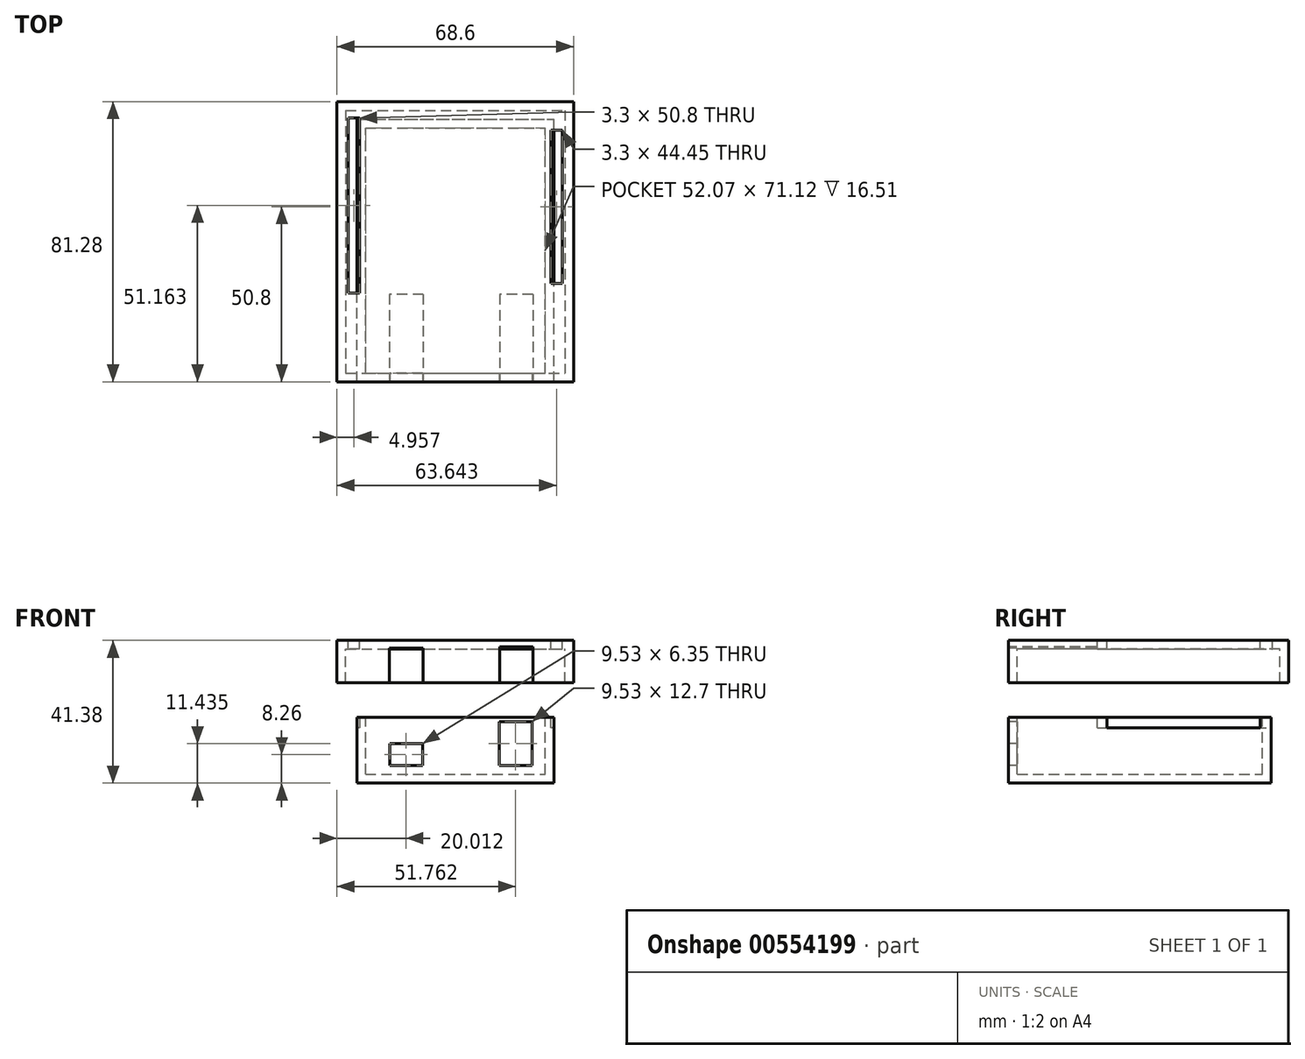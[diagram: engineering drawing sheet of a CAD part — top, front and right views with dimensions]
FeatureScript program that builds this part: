
annotation { "Feature Type Name" : "Feature", "Feature Type Description" : "" }
export const myFeature = defineFeature(function(context is Context, id is Id, definition is map)
    precondition{}
    {
        {
            var Q0;
            Q0=qCreatedBy(makeId("Front.planeOp"),FACE);
            var sketch = newSketch(context, id + "F0", { "sketchPlane" : qUnion([Q0])});
            skLineSegment(sketch, "E0.bottom", {"start": v(-28.58, -9.52) * mm, "end": v(28.58, -9.52) * mm});
            skLineSegment(sketch, "E0.top", {"start": v(-28.58, 9.52) * mm, "end": v(28.58, 9.52) * mm});
            skLineSegment(sketch, "E0.left", {"start": v(-28.58, -9.52) * mm, "end": v(-28.58, 9.52) * mm});
            skLineSegment(sketch, "E0.right", {"start": v(28.58, -9.52) * mm, "end": v(28.58, 9.52) * mm});
            skPoint(sketch, "E0.middle", {"position": v(0, 0) * mm});
            skSolve(sketch);
        }
        {
            var Q0;
            Q0 = qSketchRegion(id + "F0", true);
            extrude(context, id + "F1", {"entities" : qUnion([Q0]), "depth" : 76.2 * mm, "offsetDistance" : 25.4 * mm});
        }
        {
            var Q0;
            Q0=makeQuery(id+"F1.opExtrude","SWEPT_FACE",FACE,{"disambiguationData":[OSD([sQuery(id+"F0.wireOp",EDGE,"E0.top")])]});
            shell(context, id + "F2", {"entities" : qUnion([Q0]), "thickness" : 2.54 * mm});
        }
        {
            var Q0;
            Q0=makeQuery(id+"F1.opExtrude","CAP_FACE",FACE,{"disambiguationData":[OSD([sQuery(id+"F0.wireOp",EDGE,"E0.bottom"),sQuery(id+"F0.wireOp",EDGE,"E0.top"),sQuery(id+"F0.wireOp",EDGE,"E0.left"),sQuery(id+"F0.wireOp",EDGE,"E0.right")])],"isStart":false});
            var sketch = newSketch(context, id + "F3", { "sketchPlane" : qUnion([Q0])});
            skLineSegment(sketch, "E1.bottom", {"start": v(-9.53, -4.44) * mm, "end": v(-19.05, -4.44) * mm});
            skLineSegment(sketch, "E1.top", {"start": v(-9.53, 1.9) * mm, "end": v(-19.05, 1.9) * mm});
            skLineSegment(sketch, "E1.left", {"start": v(-9.53, -4.44) * mm, "end": v(-9.53, 1.9) * mm});
            skLineSegment(sketch, "E1.right", {"start": v(-19.05, -4.44) * mm, "end": v(-19.05, 1.9) * mm});
            skPoint(sketch, "E1.middle", {"position": v(-14.29, -1.27) * mm});
            skSolve(sketch);
        }
        {
            var Q0;
            Q0=makeQuery(id+"F3.imprint","IMPRINT",FACE,{"disambiguationData":[TD([[makeQuery(id+"F3.imprint","IMPRINT",EDGE,{"derivedFrom":sQuery(id+"F3.wireOp",EDGE,"E1.bottom")}),-1.0]])]});
            extrude(context, id + "F4", {"entities" : qUnion([Q0]), "operationType" : NewBodyOperationType.REMOVE, "oppositeDirection" : true, "depth" : 25.4 * mm, "offsetDistance" : 25.4 * mm});
        }
        {
            var Q0;
            Q0=makeQuery(id+"F1.opExtrude","CAP_FACE",FACE,{"disambiguationData":[OSD([sQuery(id+"F0.wireOp",EDGE,"E0.bottom"),sQuery(id+"F0.wireOp",EDGE,"E0.top"),sQuery(id+"F0.wireOp",EDGE,"E0.left"),sQuery(id+"F0.wireOp",EDGE,"E0.right")])],"isStart":false});
            var sketch = newSketch(context, id + "F5", { "sketchPlane" : qUnion([Q0])});
            skLineSegment(sketch, "E2.bottom", {"start": v(12.7, 8.26) * mm, "end": v(22.23, 8.26) * mm});
            skLineSegment(sketch, "E2.top", {"start": v(12.7, -4.44) * mm, "end": v(22.23, -4.44) * mm});
            skLineSegment(sketch, "E2.left", {"start": v(12.7, 8.26) * mm, "end": v(12.7, -4.44) * mm});
            skLineSegment(sketch, "E2.right", {"start": v(22.22, 8.26) * mm, "end": v(22.23, -4.44) * mm});
            skPoint(sketch, "E2.middle", {"position": v(17.46, 1.9) * mm});
            skSolve(sketch);
        }
        {
            var Q0;
            Q0=makeQuery(id+"F5.imprint","IMPRINT",FACE,{"disambiguationData":[TD([[makeQuery(id+"F5.imprint","IMPRINT",EDGE,{"derivedFrom":sQuery(id+"F5.wireOp",EDGE,"E2.bottom")}),-1.0]])]});
            extrude(context, id + "F6", {"entities" : qUnion([Q0]), "operationType" : NewBodyOperationType.REMOVE, "oppositeDirection" : true, "depth" : 25.4 * mm, "offsetDistance" : 25.4 * mm});
        }
        {
            var Q0;
            Q0=makeQuery(id+"F1.opExtrude","CAP_FACE",FACE,{"disambiguationData":[OSD([sQuery(id+"F0.wireOp",EDGE,"E0.bottom"),sQuery(id+"F0.wireOp",EDGE,"E0.top"),sQuery(id+"F0.wireOp",EDGE,"E0.left"),sQuery(id+"F0.wireOp",EDGE,"E0.right")])],"isStart":false});
            var sketch = newSketch(context, id + "F7", { "sketchPlane" : qUnion([Q0])});
            skLineSegment(sketch, "E3", {"start": v(0, 0) * mm, "end": v(0, 0) * mm});
            skSolve(sketch);
        }
        {
            var Q0;
            Q0=makeQuery(id+"F7.imprint","IMPRINT",FACE,{"disambiguationData":[TD([[makeQuery(id+"F7.imprint","IMPRINT",EDGE,{"derivedFrom":makeQuery(id+"F1.opExtrude","CAP_EDGE",EDGE,{"disambiguationData":[OSD([sQuery(id+"F0.wireOp",EDGE,"E0.bottom")])],"isStart":false})}),1.0]])]});
            var sketch = newSketch(context, id + "F8", { "sketchPlane" : qUnion([Q0])});
            skLineSegment(sketch, "E4.bottom", {"start": v(-34.3, 19.6) * mm, "end": v(34.3, 19.6) * mm});
            skLineSegment(sketch, "E4.top", {"start": v(-34.3, 31.85) * mm, "end": v(34.3, 31.85) * mm});
            skLineSegment(sketch, "E4.left", {"start": v(-34.3, 19.6) * mm, "end": v(-34.3, 31.85) * mm});
            skLineSegment(sketch, "E4.right", {"start": v(34.3, 19.6) * mm, "end": v(34.3, 31.85) * mm});
            skPoint(sketch, "E4.middle", {"position": v(0, 25.72) * mm});
            skSolve(sketch);
        }
        {
            var Q0;
            Q0 = qSketchRegion(id + "F8", true);
            extrude(context, id + "F9", {"entities" : qUnion([Q0]), "oppositeDirection" : true, "depth" : 81.28 * mm, "offsetDistance" : 25.4 * mm});
        }
        {
            var Q0;
            Q0=makeQuery(id+"F9.opExtrude","SWEPT_FACE",FACE,{"disambiguationData":[OSD([sQuery(id+"F8.wireOp",EDGE,"E4.bottom")])]});
            shell(context, id + "F10", {"entities" : qUnion([Q0]), "thickness" : 2.54 * mm});
        }
        {
            var Q0;
            Q0=makeQuery(id+"F9.opExtrude","CAP_FACE",FACE,{"disambiguationData":[OSD([sQuery(id+"F8.wireOp",EDGE,"E4.bottom"),sQuery(id+"F8.wireOp",EDGE,"E4.top"),sQuery(id+"F8.wireOp",EDGE,"E4.left"),sQuery(id+"F8.wireOp",EDGE,"E4.right")])],"isStart":true});
            var sketch = newSketch(context, id + "F11", { "sketchPlane" : qUnion([Q0])});
            skLineSegment(sketch, "E5.bottom", {"start": v(-19.15, 19.6) * mm, "end": v(-9.31, 19.6) * mm});
            skLineSegment(sketch, "E5.top", {"start": v(-19.15, 29.64) * mm, "end": v(-9.31, 29.64) * mm});
            skLineSegment(sketch, "E5.left", {"start": v(-19.15, 19.6) * mm, "end": v(-19.15, 29.64) * mm});
            skLineSegment(sketch, "E5.right", {"start": v(-9.31, 19.6) * mm, "end": v(-9.31, 29.64) * mm});
            skLineSegment(sketch, "E6.bottom", {"start": v(12.86, 19.6) * mm, "end": v(22.53, 19.6) * mm});
            skLineSegment(sketch, "E6.top", {"start": v(12.86, 29.93) * mm, "end": v(22.53, 29.93) * mm});
            skLineSegment(sketch, "E6.left", {"start": v(12.86, 19.6) * mm, "end": v(12.86, 29.93) * mm});
            skLineSegment(sketch, "E6.right", {"start": v(22.53, 19.6) * mm, "end": v(22.53, 29.93) * mm});
            skSolve(sketch);
        }
        {
            var Q0;
            Q0=makeQuery(id+"F11.imprint","IMPRINT",FACE,{"disambiguationData":[TD([[makeQuery(id+"F11.imprint","IMPRINT",EDGE,{"derivedFrom":sQuery(id+"F11.wireOp",EDGE,"E5.bottom")}),1.0]])]});
            var Q1;
            Q1=makeQuery(id+"F11.imprint","IMPRINT",FACE,{"disambiguationData":[TD([[makeQuery(id+"F11.imprint","IMPRINT",EDGE,{"derivedFrom":sQuery(id+"F11.wireOp",EDGE,"E6.bottom")}),1.0]])]});
            extrude(context, id + "F12", {"entities" : qUnion([Q0, Q1]), "operationType" : NewBodyOperationType.REMOVE, "oppositeDirection" : true, "depth" : 25.4 * mm, "offsetDistance" : 25.4 * mm});
        }
        {
            var Q0;
            Q0=makeQuery(id+"F9.opExtrude","SWEPT_FACE",FACE,{"disambiguationData":[OSD([sQuery(id+"F8.wireOp",EDGE,"E4.top")])]});
            var sketch = newSketch(context, id + "F13", { "sketchPlane" : qUnion([Q0])});
            skLineSegment(sketch, "E7.bottom", {"start": v(-31, 0.36) * mm, "end": v(-27.7, 0.36) * mm});
            skLineSegment(sketch, "E7.top", {"start": v(-31, -50.44) * mm, "end": v(-27.7, -50.44) * mm});
            skLineSegment(sketch, "E7.left", {"start": v(-31, 0.36) * mm, "end": v(-31, -50.44) * mm});
            skLineSegment(sketch, "E7.right", {"start": v(-27.7, 0.36) * mm, "end": v(-27.7, -50.44) * mm});
            skSolve(sketch);
        }
        {
            var Q0;
            Q0=makeQuery(id+"F13.imprint","IMPRINT",FACE,{"disambiguationData":[TD([[makeQuery(id+"F13.imprint","IMPRINT",EDGE,{"derivedFrom":sQuery(id+"F13.wireOp",EDGE,"E7.bottom")}),-1.0]])]});
            extrude(context, id + "F14", {"entities" : qUnion([Q0]), "operationType" : NewBodyOperationType.REMOVE, "oppositeDirection" : true, "depth" : 25.4 * mm, "offsetDistance" : 25.4 * mm});
        }
        {
            var Q0;
            Q0=makeQuery(id+"F9.opExtrude","SWEPT_FACE",FACE,{"disambiguationData":[OSD([sQuery(id+"F8.wireOp",EDGE,"E4.top")])]});
            var sketch = newSketch(context, id + "F15", { "sketchPlane" : qUnion([Q0])});
            skLineSegment(sketch, "E8.bottom", {"start": v(31, -3.17) * mm, "end": v(27.7, -3.17) * mm});
            skLineSegment(sketch, "E8.top", {"start": v(31, -47.62) * mm, "end": v(27.7, -47.62) * mm});
            skLineSegment(sketch, "E8.left", {"start": v(31, -3.17) * mm, "end": v(31, -47.62) * mm});
            skLineSegment(sketch, "E8.right", {"start": v(27.7, -3.17) * mm, "end": v(27.7, -47.62) * mm});
            skSolve(sketch);
        }
        {
            var Q0;
            Q0=makeQuery(id+"F15.imprint","IMPRINT",FACE,{"disambiguationData":[TD([[makeQuery(id+"F15.imprint","IMPRINT",EDGE,{"derivedFrom":sQuery(id+"F15.wireOp",EDGE,"E8.bottom")}),1.0]])]});
            extrude(context, id + "F16", {"entities" : qUnion([Q0]), "operationType" : NewBodyOperationType.REMOVE, "oppositeDirection" : true, "depth" : 25.4 * mm, "offsetDistance" : 25.4 * mm});
        }
    });
